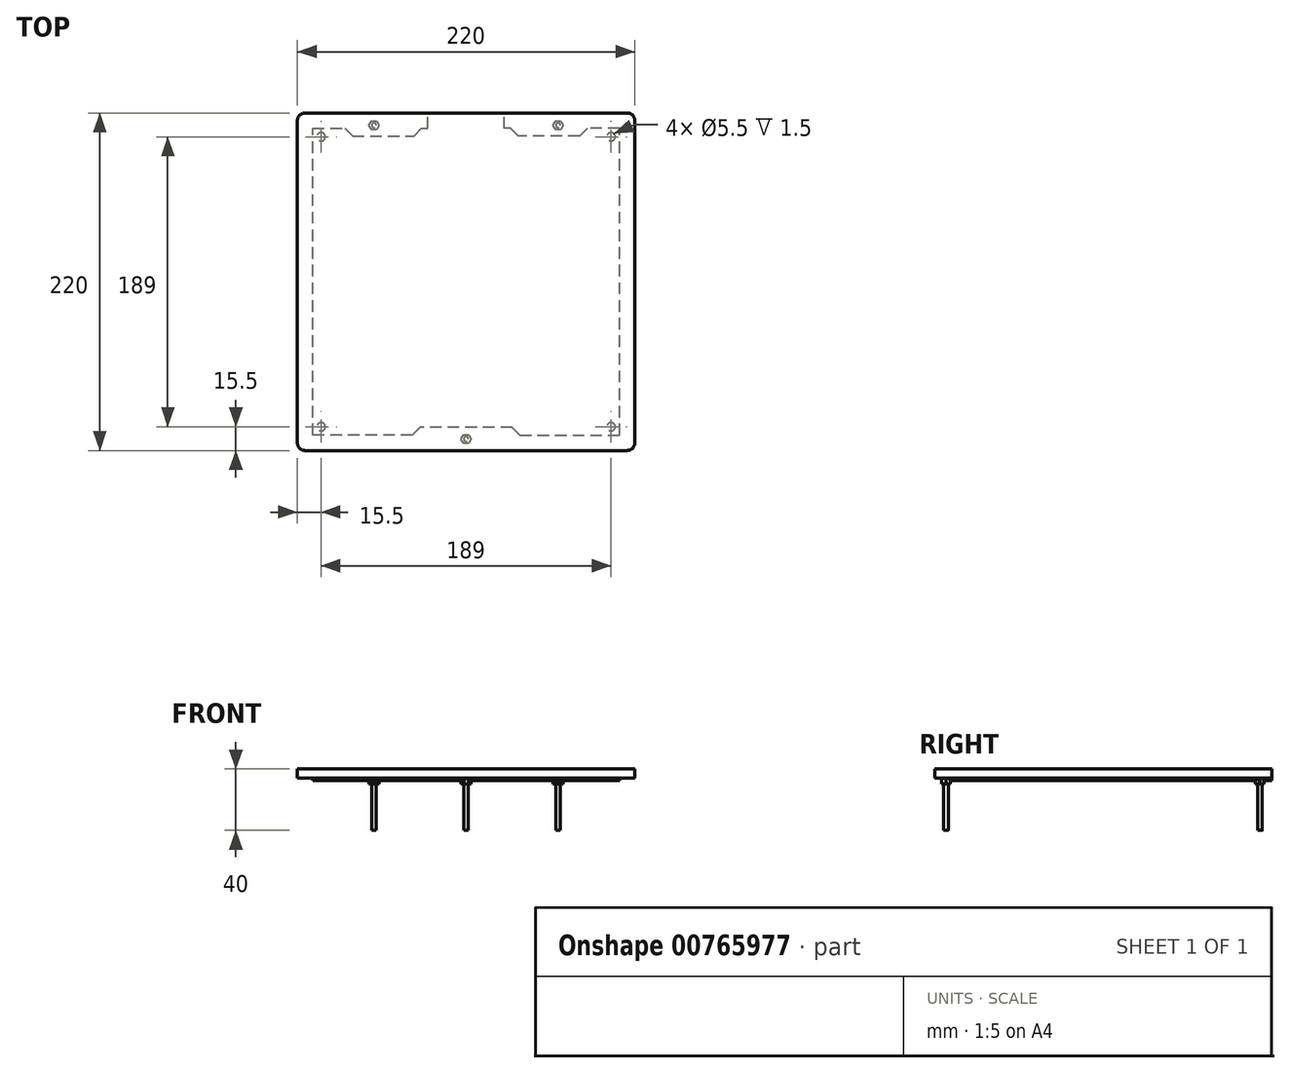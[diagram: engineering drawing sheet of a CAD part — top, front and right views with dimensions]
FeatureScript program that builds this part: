
annotation { "Feature Type Name" : "Feature", "Feature Type Description" : "" }
export const myFeature = defineFeature(function(context is Context, id is Id, definition is map)
    precondition{}
    {
        {
            var Q0;
            Q0=qCreatedBy(makeId("Top.planeOp"),FACE);
            var sketch = newSketch(context, id + "F0", { "sketchPlane" : qUnion([Q0])});
            skLineSegment(sketch, "E0.bottom", {"start": v(105, -110) * mm, "end": v(-105, -110) * mm});
            skLineSegment(sketch, "E0.top", {"start": v(105, 110) * mm, "end": v(-105, 110) * mm});
            skLineSegment(sketch, "E0.left", {"start": v(110, -105) * mm, "end": v(110, 105) * mm});
            skLineSegment(sketch, "E0.right", {"start": v(-110, -105) * mm, "end": v(-110, 105) * mm});
            skPoint(sketch, "E0.middle", {"position": v(0, 0) * mm});
            skPoint(sketch, "E1.visualSharp", {"position": v(-110, 110) * mm});
            skArc(sketch, "E1.filletArc", {"start": v(-105, 110) * mm, "mid": v(-108.54, 108.54) * mm, "end": v(-110, 105) * mm});
            skPoint(sketch, "E2.visualSharp", {"position": v(110, 110) * mm});
            skArc(sketch, "E2.filletArc", {"start": v(110, 105) * mm, "mid": v(108.54, 108.54) * mm, "end": v(105, 110) * mm});
            skPoint(sketch, "E3.visualSharp", {"position": v(110, -110) * mm});
            skArc(sketch, "E3.filletArc", {"start": v(105, -110) * mm, "mid": v(108.54, -108.54) * mm, "end": v(110, -105) * mm});
            skPoint(sketch, "E4.visualSharp", {"position": v(-110, -110) * mm});
            skArc(sketch, "E4.filletArc", {"start": v(-110, -105) * mm, "mid": v(-108.54, -108.54) * mm, "end": v(-105, -110) * mm});
            skSolve(sketch);
        }
        {
            var Q0;
            Q0 = qSketchRegion(id + "F0", true);
            extrude(context, id + "F1", {"entities" : qUnion([Q0]), "depth" : 6 * mm, "offsetDistance" : 25 * mm});
        }
        {
            var Q0;
            Q0=qCreatedBy(makeId("Top.planeOp"),FACE);
            var sketch = newSketch(context, id + "F2", { "sketchPlane" : qUnion([Q0])});
            skCircle(sketch, "E5", {"center": v(0, -102.5) * mm, "radius": 1.5 * mm});
            skCircle(sketch, "E6", {"center": v(-60, 102) * mm, "radius": 1.5 * mm});
            skCircle(sketch, "E7", {"center": v(60, 102) * mm, "radius": 1.5 * mm});
            skSolve(sketch);
        }
        {
            var Q0;
            Q0 = qSketchRegion(id + "F2", true);
            extrude(context, id + "F3", {"entities" : qUnion([Q0]), "operationType" : NewBodyOperationType.ADD, "oppositeDirection" : true, "depth" : 34 * mm, "offsetDistance" : 25 * mm});
        }
        {
            var Q0;
            Q0=qCreatedBy(makeId("Top.planeOp"),FACE);
            var sketch = newSketch(context, id + "F4", { "sketchPlane" : qUnion([Q0])});
            skCircle(sketch, "E8.cCircle", {"center": v(0, -102.5) * mm, "radius": 3.25 * mm, "construction": true});
            skLineSegment(sketch, "E8.0", {"start": v(1.63, -105.31) * mm, "end": v(-1.62, -105.31) * mm});
            skLineSegment(sketch, "E8.1", {"start": v(-1.62, -105.31) * mm, "end": v(-3.25, -102.5) * mm});
            skLineSegment(sketch, "E8.2", {"start": v(-3.25, -102.5) * mm, "end": v(-1.63, -99.69) * mm});
            skLineSegment(sketch, "E8.3", {"start": v(-1.63, -99.69) * mm, "end": v(1.62, -99.69) * mm});
            skLineSegment(sketch, "E8.4", {"start": v(1.62, -99.69) * mm, "end": v(3.25, -102.5) * mm});
            skLineSegment(sketch, "E8.5", {"start": v(3.25, -102.5) * mm, "end": v(1.62, -105.31) * mm});
            skCircle(sketch, "E9.cCircle", {"center": v(60, 102) * mm, "radius": 3.25 * mm, "construction": true});
            skLineSegment(sketch, "E9.0", {"start": v(56.75, 102) * mm, "end": v(58.38, 104.81) * mm});
            skLineSegment(sketch, "E9.1", {"start": v(58.37, 104.81) * mm, "end": v(61.62, 104.81) * mm});
            skLineSegment(sketch, "E9.2", {"start": v(61.62, 104.81) * mm, "end": v(63.25, 102) * mm});
            skLineSegment(sketch, "E9.3", {"start": v(63.25, 102) * mm, "end": v(61.62, 99.19) * mm});
            skLineSegment(sketch, "E9.4", {"start": v(61.62, 99.19) * mm, "end": v(58.37, 99.19) * mm});
            skLineSegment(sketch, "E9.5", {"start": v(58.38, 99.19) * mm, "end": v(56.75, 102) * mm});
            skCircle(sketch, "E10.cCircle", {"center": v(-60, 102) * mm, "radius": 3.25 * mm, "construction": true});
            skLineSegment(sketch, "E10.0", {"start": v(-61.62, 104.81) * mm, "end": v(-58.37, 104.81) * mm});
            skLineSegment(sketch, "E10.1", {"start": v(-58.38, 104.81) * mm, "end": v(-56.75, 102) * mm});
            skLineSegment(sketch, "E10.2", {"start": v(-56.75, 102) * mm, "end": v(-58.37, 99.19) * mm});
            skLineSegment(sketch, "E10.3", {"start": v(-58.37, 99.19) * mm, "end": v(-61.63, 99.19) * mm});
            skLineSegment(sketch, "E10.4", {"start": v(-61.62, 99.19) * mm, "end": v(-63.25, 102) * mm});
            skLineSegment(sketch, "E10.5", {"start": v(-63.25, 102) * mm, "end": v(-61.63, 104.81) * mm});
            skSolve(sketch);
        }
        {
            var Q0;
            Q0 = qSketchRegion(id + "F4", true);
            extrude(context, id + "F5", {"entities" : qUnion([Q0]), "operationType" : NewBodyOperationType.ADD, "oppositeDirection" : true, "depth" : 3.9 * mm, "offsetDistance" : 25 * mm});
        }
        {
            var Q0;
            Q0=makeQuery(id+"F1.opExtrude","CAP_FACE",FACE,{"disambiguationData":[OSD([sQuery(id+"F0.wireOp",EDGE,"E0.bottom"),sQuery(id+"F0.wireOp",EDGE,"E0.top"),sQuery(id+"F0.wireOp",EDGE,"E0.left"),sQuery(id+"F0.wireOp",EDGE,"E0.right"),sQuery(id+"F0.wireOp",EDGE,"E1.filletArc"),sQuery(id+"F0.wireOp",EDGE,"E2.filletArc"),sQuery(id+"F0.wireOp",EDGE,"E3.filletArc"),sQuery(id+"F0.wireOp",EDGE,"E4.filletArc")])],"isStart":true});
            var sketch = newSketch(context, id + "F6", { "sketchPlane" : qUnion([Q0])});
            skLineSegment(sketch, "E11.bottom", {"start": v(100, -100) * mm, "end": v(-100, -100) * mm, "construction": true});
            skLineSegment(sketch, "E11.top", {"start": v(100, 100) * mm, "end": v(-100, 100) * mm, "construction": true});
            skLineSegment(sketch, "E11.left", {"start": v(100, -100) * mm, "end": v(100, 100) * mm, "construction": true});
            skLineSegment(sketch, "E11.right", {"start": v(-100, -100) * mm, "end": v(-100, 100) * mm, "construction": true});
            skPoint(sketch, "E11.middle", {"position": v(0, 0) * mm});
            skLineSegment(sketch, "E12", {"start": v(-100, 100) * mm, "end": v(-100, -100) * mm});
            skLineSegment(sketch, "E13", {"start": v(-100, -100) * mm, "end": v(-79, -100) * mm});
            skLineSegment(sketch, "E14", {"start": v(-79, -100) * mm, "end": v(-74, -95) * mm});
            skLineSegment(sketch, "E15", {"start": v(-74, -95) * mm, "end": v(-34, -95) * mm});
            skLineSegment(sketch, "E16", {"start": v(-34, -95) * mm, "end": v(-29, -100) * mm});
            skLineSegment(sketch, "E17", {"start": v(-29, -100) * mm, "end": v(-25, -100) * mm});
            skLineSegment(sketch, "E18", {"start": v(-25, -100) * mm, "end": v(-25, -110) * mm});
            skLineSegment(sketch, "E19", {"start": v(-25, -110) * mm, "end": v(0, -110) * mm});
            skLineSegment(sketch, "E20", {"start": v(0, -110) * mm, "end": v(0, 95) * mm});
            skLineSegment(sketch, "E21", {"start": v(0, 95) * mm, "end": v(-30, 95) * mm});
            skLineSegment(sketch, "E22", {"start": v(-30, 95) * mm, "end": v(-35, 100) * mm});
            skLineSegment(sketch, "E23", {"start": v(-35, 100) * mm, "end": v(-100, 100) * mm});
            skCircle(sketch, "E24", {"center": v(-94.5, 94.5) * mm, "radius": 2.75 * mm});
            skCircle(sketch, "E25", {"center": v(-94.5, -94.5) * mm, "radius": 2.75 * mm});
            skSolve(sketch);
        }
        {
            var Q0;
            Q0 = qSketchRegion(id + "F6", true);
            extrude(context, id + "F7", {"entities" : qUnion([Q0]), "depth" : 1.5 * mm, "offsetDistance" : 25 * mm});
        }
        {
            var Q0;
            Q0=makeQuery(id+"F7.opExtrude","SWEPT_BODY",BODY,{"disambiguationData":[OSD([sQuery(id+"F6.wireOp",EDGE,"E12"),sQuery(id+"F6.wireOp",EDGE,"E13"),sQuery(id+"F6.wireOp",EDGE,"E14"),sQuery(id+"F6.wireOp",EDGE,"E15"),sQuery(id+"F6.wireOp",EDGE,"E16"),sQuery(id+"F6.wireOp",EDGE,"E17"),sQuery(id+"F6.wireOp",EDGE,"E18"),sQuery(id+"F6.wireOp",EDGE,"E19"),sQuery(id+"F6.wireOp",EDGE,"E20"),sQuery(id+"F6.wireOp",EDGE,"E21"),sQuery(id+"F6.wireOp",EDGE,"E22"),sQuery(id+"F6.wireOp",EDGE,"E23"),sQuery(id+"F6.wireOp",EDGE,"E24"),sQuery(id+"F6.wireOp",EDGE,"E25")])]});
            var Q1;
            Q1=qCreatedBy(makeId("Right.planeOp"),FACE);
            mirror(context, id + "F8", {"operationType" : NewBodyOperationType.ADD, "entities" : qUnion([Q0]), "mirrorPlane" : qUnion([Q1])});
        }
    });
